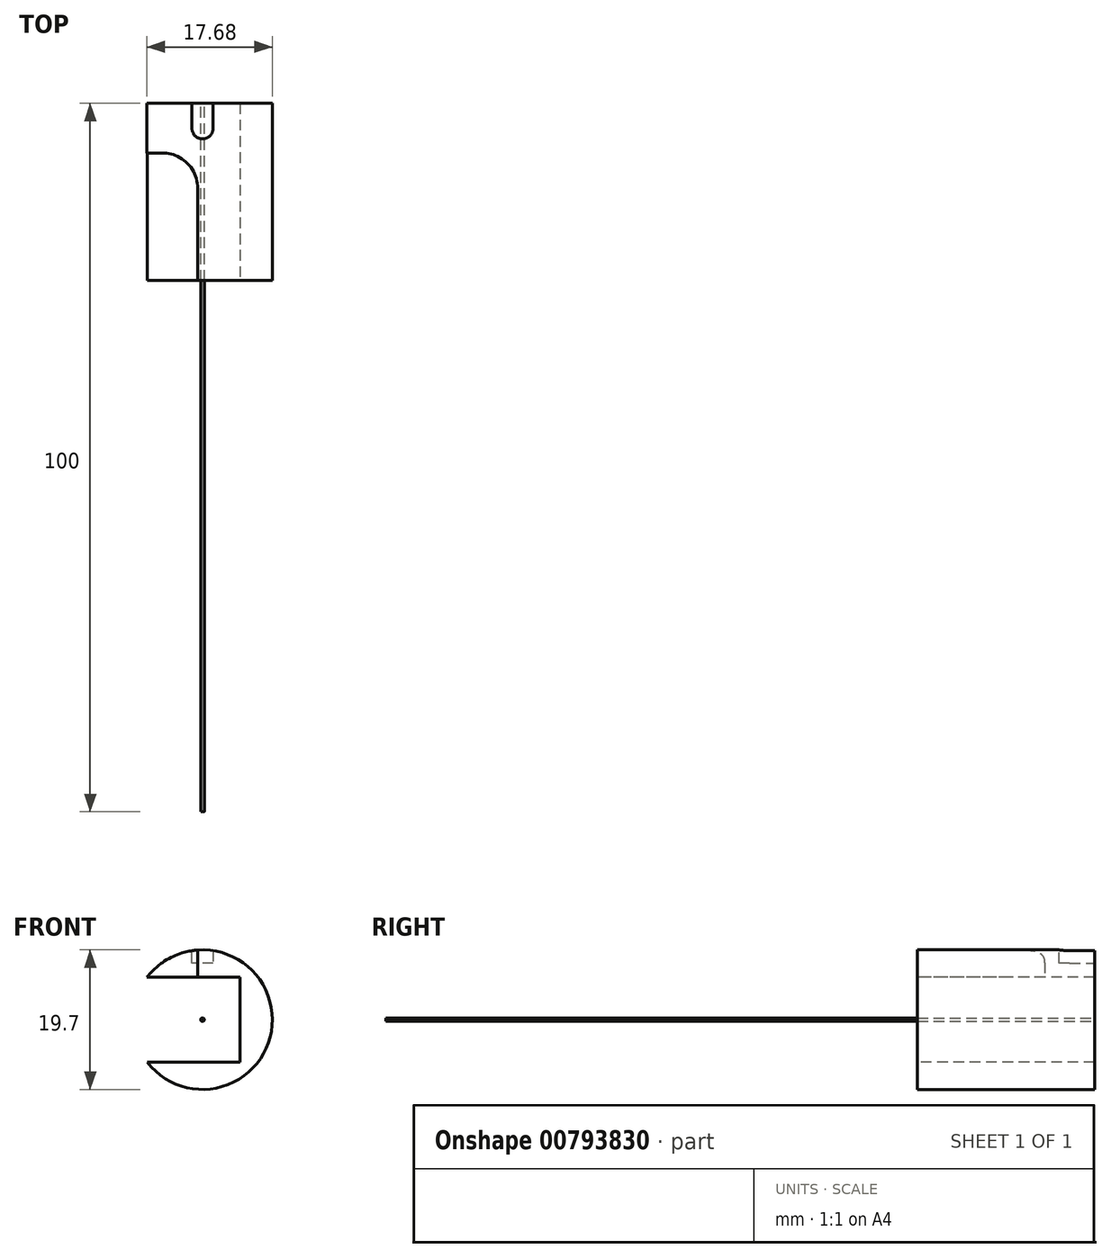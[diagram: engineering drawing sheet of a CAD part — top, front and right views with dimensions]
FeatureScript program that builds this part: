
annotation { "Feature Type Name" : "Feature", "Feature Type Description" : "" }
export const myFeature = defineFeature(function(context is Context, id is Id, definition is map)
    precondition{}
    {
        {
            var Q0;
            Q0=qCreatedBy(makeId("Front.planeOp"),FACE);
            var sketch = newSketch(context, id + "F0", { "sketchPlane" : qUnion([Q0])});
            skCircle(sketch, "E0", {"center": v(0, 0) * mm, "radius": 9.85 * mm});
            skSolve(sketch);
        }
        {
            var Q0;
            Q0=makeQuery(id+"F0.imprint","IMPRINT",FACE,{"disambiguationData":[TD([[makeQuery(id+"F0.imprint","IMPRINT",EDGE,{"derivedFrom":sQuery(id+"F0.wireOp",EDGE,"E0")}),1.0]])]});
            extrude(context, id + "F1", {"entities" : qUnion([Q0]), "oppositeDirection" : true, "depth" : 25 * mm, "offsetDistance" : 25 * mm});
        }
        {
            var Q0;
            Q0=makeQuery(id+"F1.opExtrude","CAP_FACE",FACE,{"disambiguationData":[OSD([sQuery(id+"F0.wireOp",EDGE,"E0")])],"isStart":true});
            var sketch = newSketch(context, id + "F2", { "sketchPlane" : qUnion([Q0])});
            skLineSegment(sketch, "E1.bottom", {"start": v(-12.87, 5.97) * mm, "end": v(5.3, 5.97) * mm});
            skLineSegment(sketch, "E1.top", {"start": v(-12.87, -6.03) * mm, "end": v(5.3, -6.03) * mm});
            skLineSegment(sketch, "E1.left", {"start": v(-12.87, 5.97) * mm, "end": v(-12.87, -6.03) * mm});
            skLineSegment(sketch, "E1.right", {"start": v(5.3, 5.97) * mm, "end": v(5.3, -6.03) * mm});
            skLineSegment(sketch, "E2", {"start": v(-12.87, -0.03) * mm, "end": v(5.3, -0.03) * mm, "construction": true});
            skSolve(sketch);
        }
        {
            var Q0;
            {var subQ0=sQuery(id+"F2.wireOp",EDGE,"E1.right");Q0=makeQuery(id+"F2.imprint","IMPRINT",FACE,{"disambiguationData":[TD([[makeQuery(id+"F2.imprint","IMPRINT",EDGE,{"derivedFrom":subQ0}),-1.0]])]});}
            extrude(context, id + "F3", {"entities" : qUnion([Q0]), "operationType" : NewBodyOperationType.REMOVE, "oppositeDirection" : true, "depth" : 25 * mm, "offsetDistance" : 25 * mm});
        }
        {
            var Q0;
            Q0=makeQuery(id+"F1.opExtrude","CAP_FACE",FACE,{"disambiguationData":[OSD([sQuery(id+"F0.wireOp",EDGE,"E0")])],"isStart":false});
            var sketch = newSketch(context, id + "F4", { "sketchPlane" : qUnion([Q0])});
            skLineSegment(sketch, "E3", {"start": v(-1.5, 11.97) * mm, "end": v(-1.5, 7.97) * mm});
            skLineSegment(sketch, "E4", {"start": v(-1.5, 7.97) * mm, "end": v(1.5, 7.97) * mm});
            skLineSegment(sketch, "E5", {"start": v(1.5, 7.97) * mm, "end": v(1.5, 11.97) * mm});
            skLineSegment(sketch, "E6", {"start": v(1.5, 11.97) * mm, "end": v(-1.5, 11.97) * mm});
            skLineSegment(sketch, "E7", {"start": v(0, 7.97) * mm, "end": v(0, 11.97) * mm, "construction": true});
            skSolve(sketch);
        }
        {
            var Q0;
            {var subQ0=sQuery(id+"F4.wireOp",EDGE,"E4");Q0=makeQuery(id+"F4.imprint","IMPRINT",FACE,{"disambiguationData":[TD([[makeQuery(id+"F4.imprint","IMPRINT",EDGE,{"derivedFrom":subQ0}),1.0]])]});}
            extrude(context, id + "F5", {"entities" : qUnion([Q0]), "operationType" : NewBodyOperationType.REMOVE, "oppositeDirection" : true, "depth" : 5 * mm, "offsetDistance" : 25 * mm});
        }
        {
            var Q0;
            Q0=makeQuery(id+"F5.boolean.opBoolean","COPY",EDGE,{"derivedFrom":makeQuery(id+"F5.opExtrude","CAP_EDGE",EDGE,{"disambiguationData":[OSD([sQuery(id+"F4.wireOp",EDGE,"E5")])],"isStart":false})});
            var Q1;
            Q1=makeQuery(id+"F5.boolean.opBoolean","COPY",EDGE,{"derivedFrom":makeQuery(id+"F5.opExtrude","CAP_EDGE",EDGE,{"disambiguationData":[OSD([sQuery(id+"F4.wireOp",EDGE,"E3")])],"isStart":false})});
            fillet(context, id + "F6", {"entities" : qUnion([Q0, Q1]), "radius" : 1.5 * mm, "tangentPropagation" : true, "allowEdgeOverflow" : false});
        }
        {
            var Q0;
            Q0=makeQuery(id+"F1.opExtrude","CAP_FACE",FACE,{"disambiguationData":[OSD([sQuery(id+"F0.wireOp",EDGE,"E0")])],"isStart":true});
            var sketch = newSketch(context, id + "F7", { "sketchPlane" : qUnion([Q0])});
            skLineSegment(sketch, "E8", {"start": v(-0.66, 9.83) * mm, "end": v(-0.66, 5.97) * mm});
            skSolve(sketch);
        }
        {
            var Q0;
            {var subQ0=sQuery(id+"F7.wireOp",EDGE,"E8");Q0=makeQuery(id+"F7.imprint","IMPRINT",FACE,{"disambiguationData":[TD([[makeQuery(id+"F7.imprint","IMPRINT",EDGE,{"derivedFrom":subQ0}),-1.0]])]});}
            extrude(context, id + "F8", {"entities" : qUnion([Q0]), "operationType" : NewBodyOperationType.REMOVE, "oppositeDirection" : true, "depth" : 18 * mm, "offsetDistance" : 25 * mm});
        }
        {
            var Q0;
            Q0=makeQuery(id+"F8.boolean.opBoolean","COPY",EDGE,{"derivedFrom":makeQuery(id+"F8.opExtrude","CAP_EDGE",EDGE,{"disambiguationData":[OSD([sQuery(id+"F7.wireOp",EDGE,"E8")])],"isStart":false})});
            fillet(context, id + "F9", {"entities" : qUnion([Q0]), "radius" : 5 * mm, "tangentPropagation" : true, "allowEdgeOverflow" : false});
        }
        {
            var Q0;
            Q0=makeQuery(id+"F1.opExtrude","CAP_FACE",FACE,{"disambiguationData":[OSD([sQuery(id+"F0.wireOp",EDGE,"E0")])],"isStart":false});
            var sketch = newSketch(context, id + "F10", { "sketchPlane" : qUnion([Q0])});
            skCircle(sketch, "E9", {"center": v(0, 0) * mm, "radius": 0.25 * mm});
            skSolve(sketch);
        }
        {
            var Q0;
            Q0=makeQuery(id+"F10.imprint","IMPRINT",FACE,{"disambiguationData":[TD([[makeQuery(id+"F10.imprint","IMPRINT",EDGE,{"derivedFrom":sQuery(id+"F10.wireOp",EDGE,"E9")}),1.0]])]});
            extrude(context, id + "F11", {"entities" : qUnion([Q0]), "oppositeDirection" : true, "depth" : 100 * mm, "offsetDistance" : 25 * mm});
        }
    });
